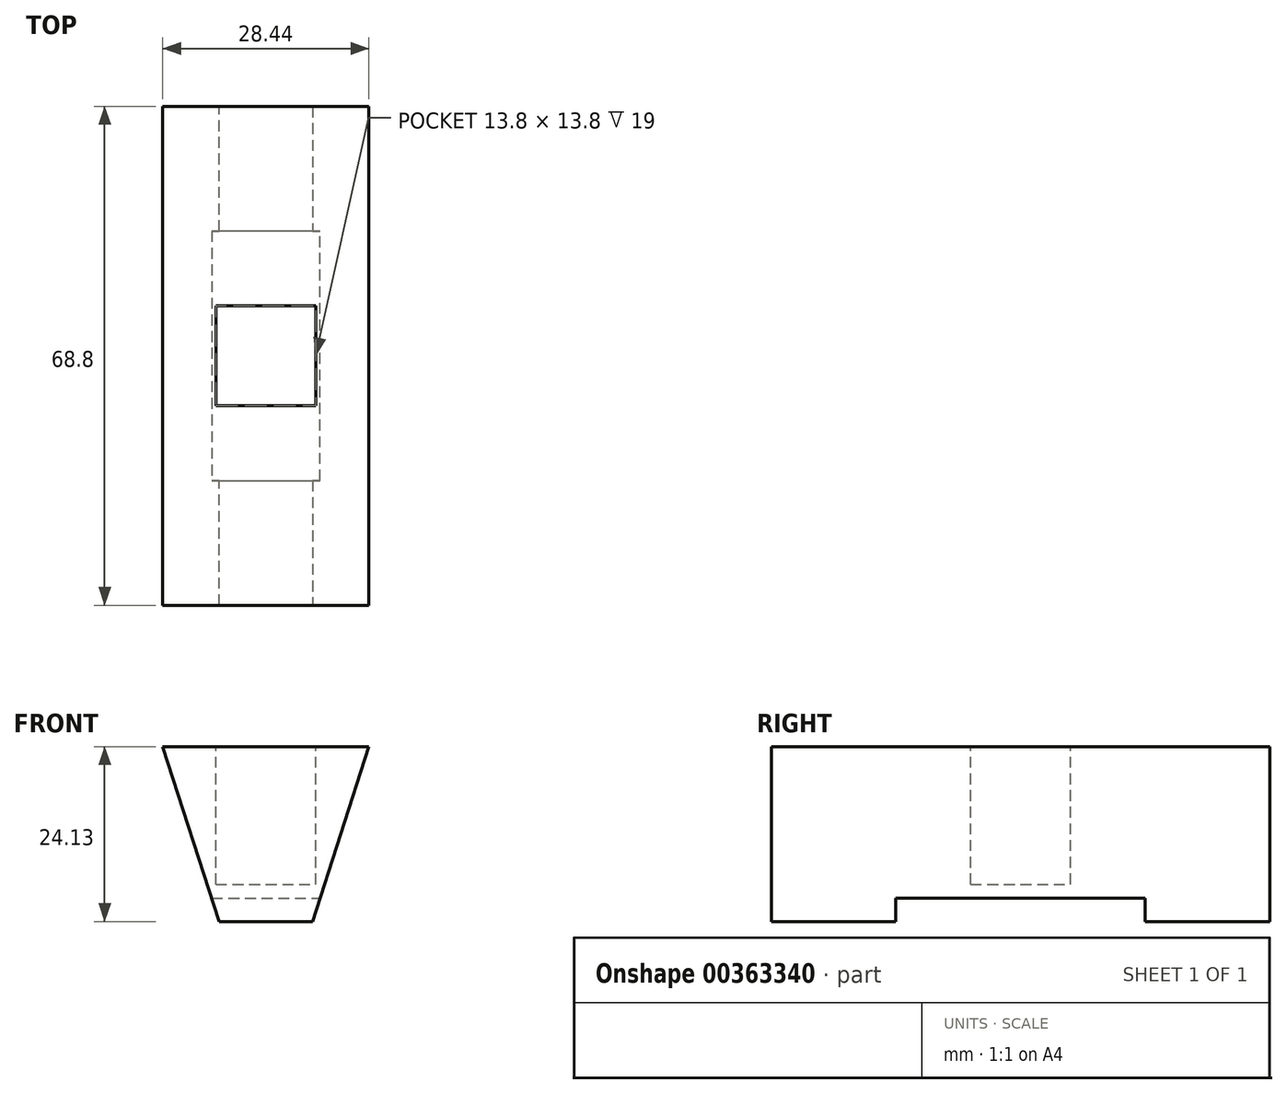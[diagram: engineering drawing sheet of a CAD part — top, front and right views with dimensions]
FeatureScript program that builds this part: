
annotation { "Feature Type Name" : "Feature", "Feature Type Description" : "" }
export const myFeature = defineFeature(function(context is Context, id is Id, definition is map)
    precondition{}
    {
        {
            var Q0;
            Q0=qCreatedBy(makeId("Top.planeOp"),FACE);
            cPlane(context, id + "F0", {"entities" : qUnion([Q0]), "cplaneType" : CPlaneType.OFFSET, "offset" : 36.12 * mm, "width" : 150 * mm, "height" : 150 * mm});
        }
        {
            var Q0;
            Q0=qCreatedBy(id+"F0.planeOp",FACE);
            var sketch = newSketch(context, id + "F1", { "sketchPlane" : qUnion([Q0])});
            skLineSegment(sketch, "E0", {"start": v(-18.1, 0) * mm, "end": v(-18.1, -68.8) * mm});
            skLineSegment(sketch, "E1", {"start": v(-18.1, -68.8) * mm, "end": v(18.1, -68.8) * mm});
            skLineSegment(sketch, "E2", {"start": v(18.1, -68.8) * mm, "end": v(18.1, 0) * mm});
            skLineSegment(sketch, "E3", {"start": v(-18.1, 0) * mm, "end": v(18.1, 0) * mm});
            skSolve(sketch);
        }
        {
            var Q0;
            Q0=qCreatedBy(makeId("Top.planeOp"),FACE);
            var sketch = newSketch(context, id + "F2", { "sketchPlane" : qUnion([Q0])});
            skLineSegment(sketch, "E4", {"start": v(6.43, 0) * mm, "end": v(6.43, -68.8) * mm});
            skLineSegment(sketch, "E5", {"start": v(6.43, -68.8) * mm, "end": v(-6.43, -68.8) * mm});
            skLineSegment(sketch, "E6", {"start": v(-6.43, -68.8) * mm, "end": v(-6.43, 0) * mm});
            skLineSegment(sketch, "E7", {"start": v(-6.43, 0) * mm, "end": v(6.43, 0) * mm});
            skSolve(sketch);
        }
        {
            var Q0;
            Q0=makeQuery(id+"F1.imprint","IMPRINT",FACE,{"disambiguationData":[TD([[makeQuery(id+"F1.imprint","IMPRINT",EDGE,{"derivedFrom":sQuery(id+"F1.wireOp",EDGE,"E0")}),1.0]])]});
            var Q1;
            Q1=makeQuery(id+"F2.imprint","IMPRINT",FACE,{"disambiguationData":[TD([[makeQuery(id+"F2.imprint","IMPRINT",EDGE,{"derivedFrom":sQuery(id+"F2.wireOp",EDGE,"E4")}),-1.0]])]});
            loft(context, id + "F3", {"sheetProfilesArray" : [{ "sheetProfileEntities" : qUnion([Q0]) }, { "sheetProfileEntities" : qUnion([Q1]) }]});
        }
        {
            var Q0;
            Q0=makeQuery(id+"F3.opLoft","CAP_FACE",FACE,{"disambiguationData":[OSD([makeQuery(id+"F1.imprint","IMPRINT",FACE,{"disambiguationData":[TD([[makeQuery(id+"F1.imprint","IMPRINT",EDGE,{"derivedFrom":sQuery(id+"F1.wireOp",EDGE,"E0")}),1.0]])]})])],"isStart":true});
            extrude(context, id + "F4", {"entities" : qUnion([Q0]), "operationType" : NewBodyOperationType.REMOVE, "oppositeDirection" : true, "depth" : 12 * mm});
        }
        {
            var Q0;
            Q0=qCreatedBy(id+"F0.planeOp",FACE);
            var sketch = newSketch(context, id + "F5", { "sketchPlane" : qUnion([Q0])});
            skLineSegment(sketch, "E8", {"start": v(-6.9, -27.5) * mm, "end": v(6.9, -27.5) * mm});
            skLineSegment(sketch, "E9", {"start": v(6.9, -27.5) * mm, "end": v(6.9, -41.3) * mm});
            skLineSegment(sketch, "E10", {"start": v(6.9, -41.3) * mm, "end": v(-6.9, -41.3) * mm});
            skLineSegment(sketch, "E11", {"start": v(-6.9, -41.3) * mm, "end": v(-6.9, -27.5) * mm});
            skSolve(sketch);
        }
        {
            var Q0;
            Q0=makeQuery(id+"F5.imprint","IMPRINT",FACE,{"disambiguationData":[TD([[makeQuery(id+"F5.imprint","IMPRINT",EDGE,{"derivedFrom":sQuery(id+"F5.wireOp",EDGE,"E8")}),-1.0]])]});
            extrude(context, id + "F6", {"entities" : qUnion([Q0]), "operationType" : NewBodyOperationType.REMOVE, "oppositeDirection" : true, "depth" : 31 * mm});
        }
        {
            var Q0;
            Q0=qCreatedBy(makeId("Top.planeOp"),FACE);
            var sketch = newSketch(context, id + "F7", { "sketchPlane" : qUnion([Q0])});
            skLineSegment(sketch, "E12", {"start": v(-10, -51.6) * mm, "end": v(10, -51.6) * mm});
            skLineSegment(sketch, "E13", {"start": v(10, -51.6) * mm, "end": v(10, -17.2) * mm});
            skLineSegment(sketch, "E14", {"start": v(10, -17.2) * mm, "end": v(-10, -17.2) * mm});
            skLineSegment(sketch, "E15", {"start": v(-10, -17.2) * mm, "end": v(-10, -51.6) * mm});
            skSolve(sketch);
        }
        {
            var Q0;
            Q0=qSketchRegion(id+"F7",true);
            extrude(context, id + "F8", {"entities" : qUnion([Q0]), "operationType" : NewBodyOperationType.REMOVE, "depth" : 3.2 * mm});
        }
    });
